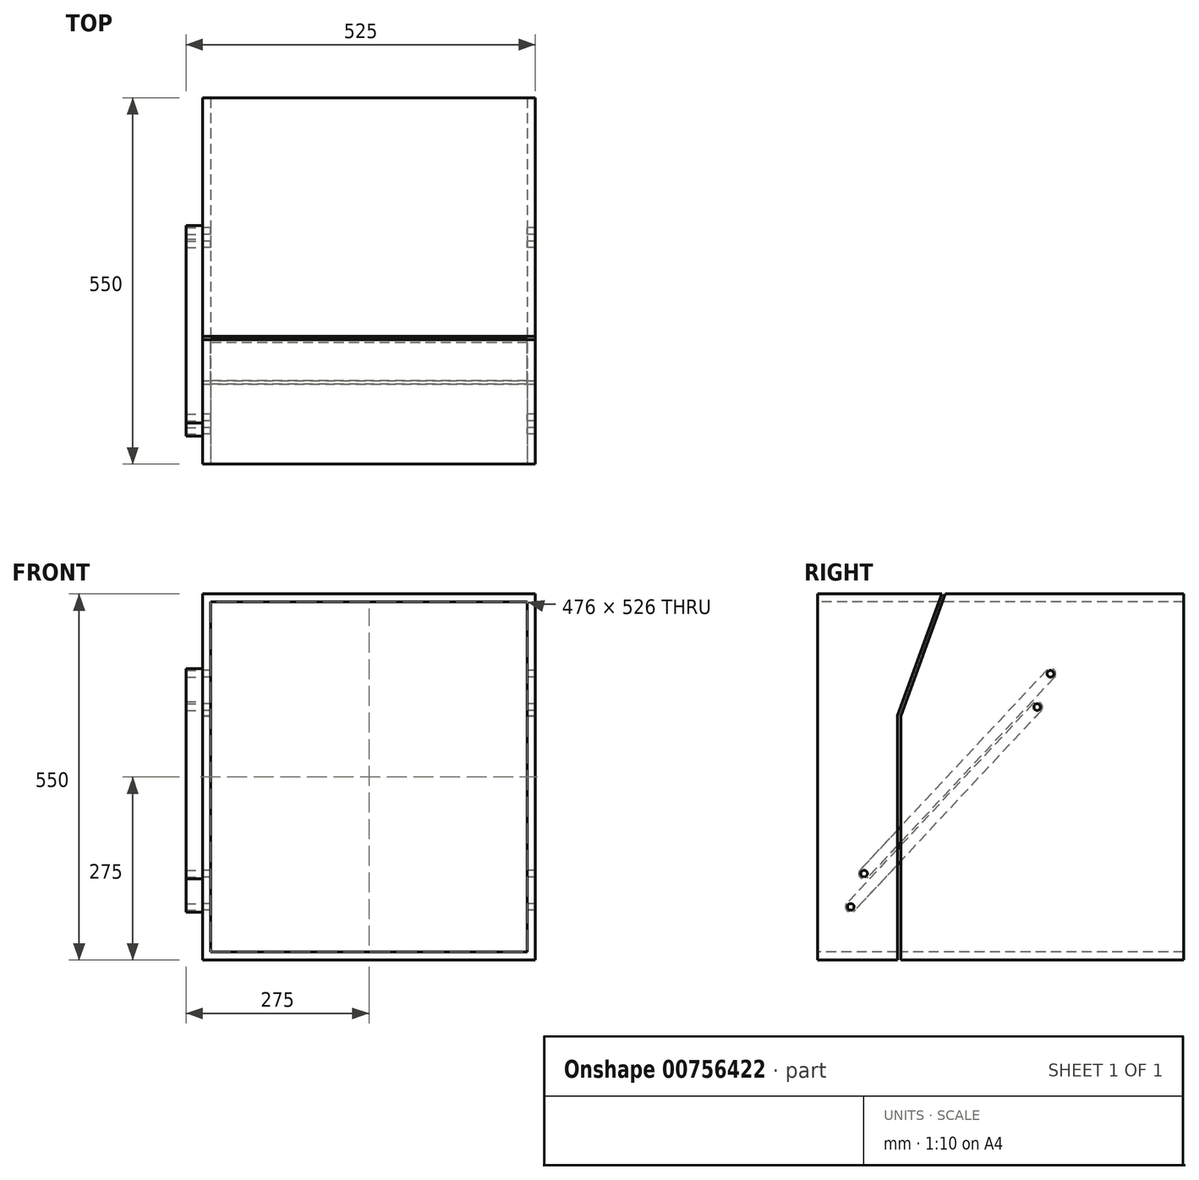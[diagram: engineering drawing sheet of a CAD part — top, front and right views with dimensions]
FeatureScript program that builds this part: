
annotation { "Feature Type Name" : "Feature", "Feature Type Description" : "" }
export const myFeature = defineFeature(function(context is Context, id is Id, definition is map)
    precondition{}
    {
        {
            var Q0;
            Q0=qCreatedBy(makeId("Top.planeOp"),FACE);
            var sketch = newSketch(context, id + "F0", { "sketchPlane" : qUnion([Q0])});
            skLineSegment(sketch, "E0.bottom", {"start": v(0, 0) * mm, "end": v(500, 0) * mm});
            skLineSegment(sketch, "E0.top", {"start": v(0, 550) * mm, "end": v(500, 550) * mm});
            skLineSegment(sketch, "E0.left", {"start": v(0, 0) * mm, "end": v(0, 550) * mm});
            skLineSegment(sketch, "E0.right", {"start": v(500, 0) * mm, "end": v(500, 550) * mm});
            skSolve(sketch);
        }
        {
            var Q0;
            Q0=makeQuery(id+"F0.imprint","IMPRINT",FACE,{"disambiguationData":[TD([[makeQuery(id+"F0.imprint","IMPRINT",EDGE,{"derivedFrom":sQuery(id+"F0.wireOp",EDGE,"E0.bottom")}),1.0]])]});
            extrude(context, id + "F1", {"entities" : qUnion([Q0]), "depth" : 550 * mm, "offsetDistance" : 25 * mm});
        }
        {
            var Q0;
            Q0=makeQuery(id+"F1.opExtrude","SWEPT_FACE",FACE,{"disambiguationData":[OSD([sQuery(id+"F0.wireOp",EDGE,"E0.right")])]});
            var sketch = newSketch(context, id + "F2", { "sketchPlane" : qUnion([Q0])});
            skLineSegment(sketch, "E1", {"start": v(119.99, 0) * mm, "end": v(119.99, 367.41) * mm});
            skLineSegment(sketch, "E2", {"start": v(119.99, 367.41) * mm, "end": v(186.76, 550) * mm});
            skLineSegment(sketch, "E3.0", {"start": v(124.99, 366.53) * mm, "end": v(192.08, 550) * mm});
            skLineSegment(sketch, "E3.1", {"start": v(124.99, 0) * mm, "end": v(124.99, 366.53) * mm});
            skSolve(sketch);
        }
        {
            var Q0;
            {var subQ3=sQuery(id+"F2.wireOp",EDGE,"E1");Q0=makeQuery(id+"F2.imprint","IMPRINT",FACE,{"disambiguationData":[TD([[makeQuery(id+"F2.imprint","IMPRINT",EDGE,{"derivedFrom":subQ3}),-1.0]])]});}
            extrude(context, id + "F3", {"entities" : qUnion([Q0]), "operationType" : NewBodyOperationType.REMOVE, "oppositeDirection" : true, "depth" : 588 * mm, "offsetDistance" : 25 * mm});
        }
        {
            var Q0;
            Q0=makeQuery(id+"F1.opExtrude","SWEPT_FACE",FACE,{"disambiguationData":[OSD([sQuery(id+"F0.wireOp",EDGE,"E0.bottom")])]});
            var sketch = newSketch(context, id + "F4", { "sketchPlane" : qUnion([Q0])});
            skLineSegment(sketch, "E4", {"start": v(0, 550) * mm, "end": v(12, 550) * mm});
            skLineSegment(sketch, "E5", {"start": v(12, 550) * mm, "end": v(12, 538) * mm});
            skLineSegment(sketch, "E6", {"start": v(500, 0) * mm, "end": v(500, 12) * mm});
            skLineSegment(sketch, "E7", {"start": v(500, 12) * mm, "end": v(488, 12) * mm});
            skLineSegment(sketch, "E8.bottom", {"start": v(12, 538) * mm, "end": v(488, 538) * mm});
            skLineSegment(sketch, "E8.top", {"start": v(12, 12) * mm, "end": v(488, 12) * mm});
            skLineSegment(sketch, "E8.left", {"start": v(12, 538) * mm, "end": v(12, 12) * mm});
            skLineSegment(sketch, "E8.right", {"start": v(488, 538) * mm, "end": v(488, 12) * mm});
            skSolve(sketch);
        }
        {
            var Q0;
            Q0=makeQuery(id+"F4.imprint","IMPRINT",FACE,{"disambiguationData":[TD([[makeQuery(id+"F4.imprint","IMPRINT",EDGE,{"derivedFrom":sQuery(id+"F4.wireOp",EDGE,"E8.bottom")}),-1.0]])]});
            extrude(context, id + "F5", {"entities" : qUnion([Q0]), "operationType" : NewBodyOperationType.REMOVE, "endBound" : BoundingType.THROUGH_ALL, "oppositeDirection" : true, "depth" : 25 * mm, "offsetDistance" : 25 * mm});
        }
        {
            var Q0;
            {var subQ0=sQuery(id+"F0.wireOp",EDGE,"E0.top");var subQ2=sQuery(id+"F0.wireOp",EDGE,"E0.left");Q0=makeQuery(id+"F3.boolean.opBoolean","SPLIT",FACE,{"disambiguationData":[TD([makeQuery(id+"F1.opExtrude","SWEPT_FACE",FACE,{"disambiguationData":[OSD([subQ0])]})])],"derivedFrom":makeQuery(id+"F1.opExtrude","SWEPT_FACE",FACE,{"disambiguationData":[OSD([subQ2])]})});}
            var sketch = newSketch(context, id + "F6", { "sketchPlane" : qUnion([Q0])});
            skLineSegment(sketch, "E9", {"start": v(-550, 550) * mm, "end": v(-424.27, 550) * mm});
            skLineSegment(sketch, "E10", {"start": v(-550, 550) * mm, "end": v(-350, 550) * mm});
            skLineSegment(sketch, "E11", {"start": v(-350, 550) * mm, "end": v(-350, 430) * mm, "construction": true});
            skLineSegment(sketch, "E12", {"start": v(-350, 430) * mm, "end": v(-350, 380) * mm, "construction": true});
            skLineSegment(sketch, "E13", {"start": v(-350, 380) * mm, "end": v(-330, 380) * mm, "construction": true});
            skCircle(sketch, "E14", {"center": v(-350, 430) * mm, "radius": 5 * mm});
            skCircle(sketch, "E15", {"center": v(-330, 380) * mm, "radius": 5 * mm});
            skLineSegment(sketch, "E16", {"start": v(0, 0) * mm, "end": v(-50, 0) * mm});
            skLineSegment(sketch, "E17", {"start": v(-50, 0) * mm, "end": v(-50, 80) * mm, "construction": true});
            skLineSegment(sketch, "E18", {"start": v(-50, 80) * mm, "end": v(-70, 80) * mm, "construction": true});
            skLineSegment(sketch, "E19", {"start": v(-70, 80) * mm, "end": v(-70, 130) * mm, "construction": true});
            skCircle(sketch, "E20", {"center": v(-70, 130) * mm, "radius": 5 * mm});
            skCircle(sketch, "E21", {"center": v(-50, 80) * mm, "radius": 5 * mm});
            skLineSegment(sketch, "E22", {"start": v(-350, 430) * mm, "end": v(-70, 130) * mm, "construction": true});
            skLineSegment(sketch, "E23", {"start": v(-330, 380) * mm, "end": v(-50, 80) * mm, "construction": true});
            skLineSegment(sketch, "E24.0", {"start": v(-335.85, 374.54) * mm, "end": v(-55.85, 74.54) * mm});
            skLineSegment(sketch, "E25.0", {"start": v(-324.15, 385.46) * mm, "end": v(-44.15, 85.46) * mm});
            skLineSegment(sketch, "E26.0", {"start": v(-355.85, 424.54) * mm, "end": v(-75.85, 124.54) * mm});
            skLineSegment(sketch, "E27.0", {"start": v(-344.15, 435.46) * mm, "end": v(-64.15, 135.46) * mm});
            skArc(sketch, "E28", {"start": v(-75.85, 124.54) * mm, "mid": v(-64.54, 124.15) * mm, "end": v(-64.15, 135.46) * mm});
            skArc(sketch, "E29", {"start": v(-55.85, 74.54) * mm, "mid": v(-44.54, 74.15) * mm, "end": v(-44.15, 85.46) * mm});
            skArc(sketch, "E30", {"start": v(-344.15, 435.46) * mm, "mid": v(-355.46, 435.85) * mm, "end": v(-355.85, 424.54) * mm});
            skArc(sketch, "E31", {"start": v(-324.15, 385.46) * mm, "mid": v(-335.46, 385.85) * mm, "end": v(-335.85, 374.54) * mm});
            skLineSegment(sketch, "E32", {"start": v(-330, 380) * mm, "end": v(-324.15, 385.46) * mm, "construction": true});
            skLineSegment(sketch, "E33", {"start": v(-350, 430) * mm, "end": v(-344.15, 435.46) * mm, "construction": true});
            skSolve(sketch);
        }
        {
            var Q0;
            Q0=makeQuery(id+"F6.imprint","IMPRINT",FACE,{"disambiguationData":[TD([[makeQuery(id+"F6.imprint","IMPRINT",EDGE,{"derivedFrom":sQuery(id+"F6.wireOp",EDGE,"E20")}),-1.0]])]});
            var Q1;
            Q1=makeQuery(id+"F6.imprint","IMPRINT",FACE,{"disambiguationData":[TD([[makeQuery(id+"F6.imprint","IMPRINT",EDGE,{"derivedFrom":sQuery(id+"F6.wireOp",EDGE,"E21")}),-1.0]])]});
            var Q2;
            Q2=makeQuery(id+"F6.imprint","IMPRINT",FACE,{"disambiguationData":[TD([[makeQuery(id+"F6.imprint","IMPRINT",EDGE,{"derivedFrom":sQuery(id+"F6.wireOp",EDGE,"E15")}),-1.0]])]});
            var Q3;
            Q3=makeQuery(id+"F6.imprint","IMPRINT",FACE,{"disambiguationData":[TD([[makeQuery(id+"F6.imprint","IMPRINT",EDGE,{"derivedFrom":sQuery(id+"F6.wireOp",EDGE,"E14")}),-1.0]])]});
            extrude(context, id + "F7", {"entities" : qUnion([Q0, Q1, Q2, Q3]), "depth" : 25 * mm, "offsetDistance" : 25 * mm});
        }
        {
            var Q0;
            Q0=makeQuery(id+"F6.imprint","IMPRINT",FACE,{"disambiguationData":[TD([[makeQuery(id+"F6.imprint","IMPRINT",EDGE,{"derivedFrom":sQuery(id+"F6.wireOp",EDGE,"E14")}),1.0]])]});
            var Q1;
            Q1=makeQuery(id+"F6.imprint","IMPRINT",FACE,{"disambiguationData":[TD([[makeQuery(id+"F6.imprint","IMPRINT",EDGE,{"derivedFrom":sQuery(id+"F6.wireOp",EDGE,"E15")}),1.0]])]});
            var Q2;
            Q2=makeQuery(id+"F6.imprint","IMPRINT",FACE,{"disambiguationData":[TD([[makeQuery(id+"F6.imprint","IMPRINT",EDGE,{"derivedFrom":sQuery(id+"F6.wireOp",EDGE,"E20")}),1.0]])]});
            var Q3;
            Q3=makeQuery(id+"F6.imprint","IMPRINT",FACE,{"disambiguationData":[TD([[makeQuery(id+"F6.imprint","IMPRINT",EDGE,{"derivedFrom":sQuery(id+"F6.wireOp",EDGE,"E21")}),1.0]])]});
            extrude(context, id + "F8", {"entities" : qUnion([Q0, Q1, Q2, Q3]), "operationType" : NewBodyOperationType.REMOVE, "oppositeDirection" : true, "depth" : 1105 * mm, "offsetDistance" : 25 * mm});
        }
    });
